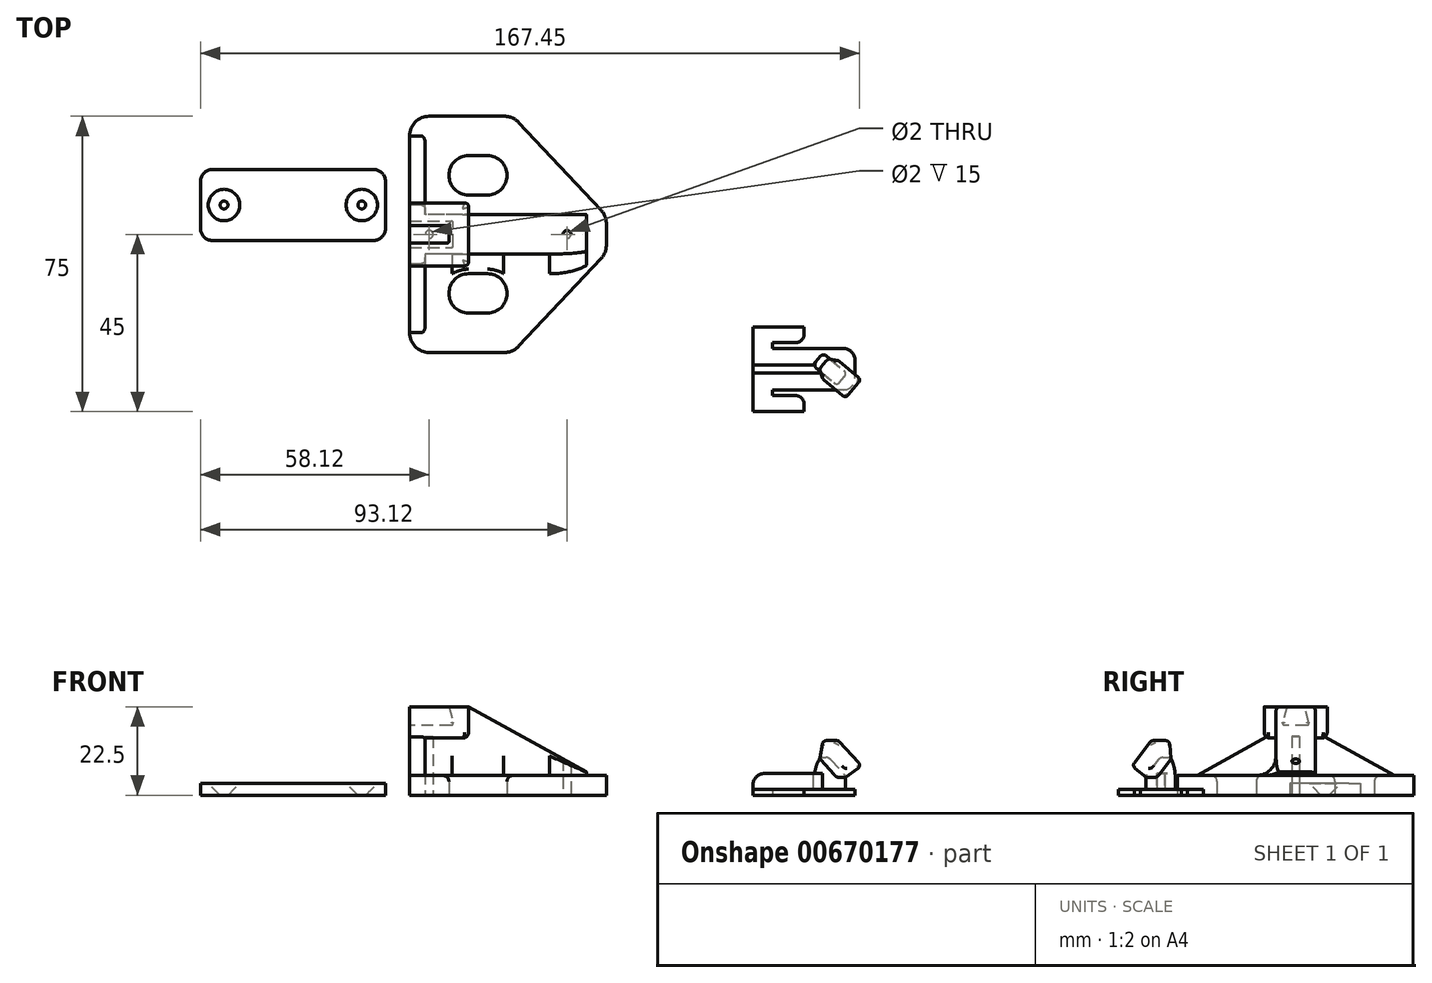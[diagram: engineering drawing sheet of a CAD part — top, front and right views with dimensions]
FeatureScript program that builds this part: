
annotation { "Feature Type Name" : "Feature", "Feature Type Description" : "" }
export const myFeature = defineFeature(function(context is Context, id is Id, definition is map)
    precondition{}
    {
        {
            var Q0;
            Q0=qCreatedBy(makeId("Front.planeOp"),FACE);
            var sketch = newSketch(context, id + "F0", { "sketchPlane" : qUnion([Q0])});
            skLineSegment(sketch, "E0.bottom", {"start": v(-57, 22.5) * mm, "end": v(-42, 22.5) * mm});
            skLineSegment(sketch, "E0.left", {"start": v(-57, 22.5) * mm, "end": v(-57, 0) * mm});
            skLineSegment(sketch, "E1", {"start": v(-42, 22.5) * mm, "end": v(-12, 5.88) * mm});
            skLineSegment(sketch, "E2", {"start": v(-12, 5.88) * mm, "end": v(-12, 0) * mm});
            skLineSegment(sketch, "E3", {"start": v(-12, 0) * mm, "end": v(-57, 0) * mm});
            skSolve(sketch);
        }
        {
            var Q0;
            Q0=makeQuery(id+"F0.imprint","IMPRINT",FACE,{"disambiguationData":[TD([[makeQuery(id+"F0.imprint","IMPRINT",EDGE,{"derivedFrom":sQuery(id+"F0.wireOp",EDGE,"E0.bottom")}),-1.0]])]});
            extrude(context, id + "F1", {"entities" : qUnion([Q0]), "depth" : 10 * mm, "offsetDistance" : 25 * mm, "symmetric" : true});
        }
        {
            var Q0;
            Q0=qCreatedBy(makeId("Top.planeOp"),FACE);
            var sketch = newSketch(context, id + "F2", { "sketchPlane" : qUnion([Q0])});
            skLineSegment(sketch, "E4", {"start": v(-57, 0) * mm, "end": v(-57, -25) * mm});
            skLineSegment(sketch, "E5", {"start": v(-52, -30) * mm, "end": v(-32.9, -30) * mm});
            skLineSegment(sketch, "E6", {"start": v(-29.25, -28.42) * mm, "end": v(-8.35, -6.16) * mm});
            skLineSegment(sketch, "E7", {"start": v(-7, -2.74) * mm, "end": v(-7, 0) * mm});
            skLineSegment(sketch, "E8", {"start": v(-7, 0) * mm, "end": v(-57, 0) * mm});
            skPoint(sketch, "E9.visualSharp", {"position": v(-57, -30) * mm});
            skArc(sketch, "E9.filletArc", {"start": v(-57, -25) * mm, "mid": v(-55.54, -28.54) * mm, "end": v(-52, -30) * mm});
            skPoint(sketch, "E10.visualSharp", {"position": v(-30.73, -30) * mm});
            skArc(sketch, "E10.filletArc", {"start": v(-32.9, -30) * mm, "mid": v(-30.9, -29.59) * mm, "end": v(-29.25, -28.42) * mm});
            skPoint(sketch, "E11.visualSharp", {"position": v(-7, -4.72) * mm});
            skArc(sketch, "E11.filletArc", {"start": v(-8.35, -6.16) * mm, "mid": v(-7.35, -4.58) * mm, "end": v(-7, -2.74) * mm});
            skLineSegment(sketch, "E12.0", {"start": v(-47, -15) * mm, "end": v(-47, -15) * mm});
            skLineSegment(sketch, "E12.1", {"start": v(-37.22, -10) * mm, "end": v(-42, -10) * mm});
            skLineSegment(sketch, "E12.2", {"start": v(-33.58, -18.42) * mm, "end": v(-33.58, -18.42) * mm});
            skLineSegment(sketch, "E12.3", {"start": v(-42, -20) * mm, "end": v(-37.22, -20) * mm});
            skPoint(sketch, "E13.visualSharp", {"position": v(-25.67, -10) * mm});
            skArc(sketch, "E13.filletArc", {"start": v(-33.58, -18.42) * mm, "mid": v(-32.63, -13.01) * mm, "end": v(-37.22, -10) * mm});
            skPoint(sketch, "E14.visualSharp", {"position": v(-47, -10) * mm});
            skArc(sketch, "E14.filletArc", {"start": v(-42, -10) * mm, "mid": v(-45.54, -11.46) * mm, "end": v(-47, -15) * mm});
            skPoint(sketch, "E15.visualSharp", {"position": v(-47, -20) * mm});
            skArc(sketch, "E15.filletArc", {"start": v(-47, -15) * mm, "mid": v(-45.54, -18.54) * mm, "end": v(-42, -20) * mm});
            skPoint(sketch, "E16.visualSharp", {"position": v(-35.06, -20) * mm});
            skArc(sketch, "E16.filletArc", {"start": v(-37.22, -20) * mm, "mid": v(-35.24, -19.59) * mm, "end": v(-33.58, -18.42) * mm});
            skSolve(sketch);
        }
        {
            var Q0;
            Q0=makeQuery(id+"F2.imprint","IMPRINT",FACE,{"disambiguationData":[TD([[makeQuery(id+"F2.imprint","IMPRINT",EDGE,{"derivedFrom":sQuery(id+"F2.wireOp",EDGE,"E4")}),1.0]])]});
            extrude(context, id + "F3", {"entities" : qUnion([Q0]), "operationType" : NewBodyOperationType.ADD, "depth" : 5 * mm, "offsetDistance" : 25 * mm});
        }
        {
            var Q0;
            Q0=makeQuery(id+"F1.opExtrude","SWEPT_BODY",BODY,{"disambiguationData":[OSD([sQuery(id+"F0.wireOp",EDGE,"E0.bottom"),sQuery(id+"F0.wireOp",EDGE,"E0.top"),sQuery(id+"F0.wireOp",EDGE,"E0.left"),sQuery(id+"F0.wireOp",EDGE,"E0.right")])]});
            var Q1;
            Q1=qCreatedBy(makeId("Front.planeOp"),FACE);
            mirror(context, id + "F4", {"operationType" : NewBodyOperationType.ADD, "entities" : qUnion([Q0]), "mirrorPlane" : qUnion([Q1])});
        }
        {
            var Q0;
            Q0=makeQuery(id+"F3.opExtrude","CAP_EDGE",EDGE,{"disambiguationData":[OSD([sQuery(id+"F2.wireOp",EDGE,"E15.filletArc")])],"isStart":false});
            var Q1;
            Q1=makeQuery(id+"F4.opPattern","COPY",EDGE,{"derivedFrom":makeQuery(id+"F3.opExtrude","CAP_EDGE",EDGE,{"disambiguationData":[OSD([sQuery(id+"F2.wireOp",EDGE,"E14.filletArc")])],"isStart":false}),"instanceName":"1"});
            fillet(context, id + "F5", {"entities" : qUnion([Q0, Q1]), "radius" : 1.5 * mm, "tangentPropagation" : true, "allowEdgeOverflow" : false});
        }
        {
            var Q0;
            {var subQ0=makeQuery(id+"F3.boolean.opBoolean","MERGE",FACE,{"derivedFrom":[makeQuery(id+"F1.opExtrude","SWEPT_FACE",FACE,{"disambiguationData":[OSD([sQuery(id+"F0.wireOp",EDGE,"E3")])]}),makeQuery(id+"F3.opExtrude","CAP_FACE",FACE,{"disambiguationData":[OSD([sQuery(id+"F2.wireOp",EDGE,"E4"),sQuery(id+"F2.wireOp",EDGE,"E5"),sQuery(id+"F2.wireOp",EDGE,"E6"),sQuery(id+"F2.wireOp",EDGE,"E7"),sQuery(id+"F2.wireOp",EDGE,"E8"),sQuery(id+"F2.wireOp",EDGE,"E9.filletArc"),sQuery(id+"F2.wireOp",EDGE,"E10.filletArc"),sQuery(id+"F2.wireOp",EDGE,"E11.filletArc"),sQuery(id+"F2.wireOp",EDGE,"E12.0"),sQuery(id+"F2.wireOp",EDGE,"E12.1"),sQuery(id+"F2.wireOp",EDGE,"E12.2"),sQuery(id+"F2.wireOp",EDGE,"E12.3"),sQuery(id+"F2.wireOp",EDGE,"E13.filletArc"),sQuery(id+"F2.wireOp",EDGE,"E14.filletArc"),sQuery(id+"F2.wireOp",EDGE,"E15.filletArc"),sQuery(id+"F2.wireOp",EDGE,"E16.filletArc")])],"isStart":true})]});Q0=makeQuery(id+"F4.boolean.opBoolean","MERGE",FACE,{"derivedFrom":[subQ0,makeQuery(id+"F4.opPattern","COPY",FACE,{"derivedFrom":subQ0,"instanceName":"1"})]});}
            var sketch = newSketch(context, id + "F6", { "sketchPlane" : qUnion([Q0])});
            skLineSegment(sketch, "E17", {"start": v(-57, 0) * mm, "end": v(-7, 0) * mm, "construction": true});
            skCircle(sketch, "E18", {"center": v(-52, 0) * mm, "radius": 1 * mm});
            skCircle(sketch, "E19", {"center": v(-17, 0) * mm, "radius": 1 * mm});
            skSolve(sketch);
        }
        {
            var Q0;
            Q0=makeQuery(id+"F6.imprint","IMPRINT",FACE,{"disambiguationData":[TD([[makeQuery(id+"F6.imprint","IMPRINT",EDGE,{"derivedFrom":sQuery(id+"F6.wireOp",EDGE,"E18")}),1.0]])]});
            var Q1;
            Q1=makeQuery(id+"F6.imprint","IMPRINT",FACE,{"disambiguationData":[TD([[makeQuery(id+"F6.imprint","IMPRINT",EDGE,{"derivedFrom":sQuery(id+"F6.wireOp",EDGE,"E19")}),1.0]])]});
            extrude(context, id + "F7", {"entities" : qUnion([Q0, Q1]), "operationType" : NewBodyOperationType.REMOVE, "oppositeDirection" : true, "depth" : 15 * mm, "offsetDistance" : 25 * mm});
        }
        {
            var Q0;
            {var subQ0=makeQuery(id+"F3.boolean.opBoolean","MERGE",FACE,{"derivedFrom":[makeQuery(id+"F1.opExtrude","SWEPT_FACE",FACE,{"disambiguationData":[OSD([sQuery(id+"F0.wireOp",EDGE,"E0.left")])]}),makeQuery(id+"F3.opExtrude","SWEPT_FACE",FACE,{"disambiguationData":[OSD([sQuery(id+"F2.wireOp",EDGE,"E4")])]})]});Q0=makeQuery(id+"F4.boolean.opBoolean","MERGE",FACE,{"derivedFrom":[subQ0,makeQuery(id+"F4.opPattern","COPY",FACE,{"derivedFrom":subQ0,"instanceName":"1"})]});}
            var sketch = newSketch(context, id + "F8", { "sketchPlane" : qUnion([Q0])});
            skLineSegment(sketch, "E20.bottom", {"start": v(-8, 22.5) * mm, "end": v(8, 22.5) * mm});
            skLineSegment(sketch, "E20.top", {"start": v(-8, 14.5) * mm, "end": v(8, 14.5) * mm});
            skLineSegment(sketch, "E20.left", {"start": v(-8, 22.5) * mm, "end": v(-8, 14.5) * mm});
            skLineSegment(sketch, "E20.right", {"start": v(8, 22.5) * mm, "end": v(8, 14.5) * mm});
            skLineSegment(sketch, "E21", {"start": v(-25, 5) * mm, "end": v(25, 5) * mm});
            skLineSegment(sketch, "E22", {"start": v(-8, 14.5) * mm, "end": v(-25, 5) * mm});
            skLineSegment(sketch, "E23", {"start": v(25, 5) * mm, "end": v(8, 14.5) * mm});
            skSolve(sketch);
        }
        {
            var Q0;
            {var subQ0=sQuery(id+"F8.wireOp",EDGE,"E22");Q0=makeQuery(id+"F8.imprint","IMPRINT",FACE,{"disambiguationData":[TD([[makeQuery(id+"F8.imprint","IMPRINT",EDGE,{"derivedFrom":subQ0}),1.0]])]});}
            var Q1;
            {var subQ0=sQuery(id+"F8.wireOp",EDGE,"E23");Q1=makeQuery(id+"F8.imprint","IMPRINT",FACE,{"disambiguationData":[TD([[makeQuery(id+"F8.imprint","IMPRINT",EDGE,{"derivedFrom":subQ0}),1.0]])]});}
            extrude(context, id + "F9", {"entities" : qUnion([Q0, Q1]), "operationType" : NewBodyOperationType.ADD, "oppositeDirection" : true, "depth" : 4 * mm, "offsetDistance" : 25 * mm});
        }
        {
            var Q0;
            {var subQ3=sQuery(id+"F8.wireOp",EDGE,"E20.left");Q0=makeQuery(id+"F8.imprint","IMPRINT",FACE,{"disambiguationData":[TD([[makeQuery(id+"F8.imprint","IMPRINT",EDGE,{"derivedFrom":subQ3}),1.0]])]});}
            var Q1;
            {var subQ3=sQuery(id+"F8.wireOp",EDGE,"E20.right");Q1=makeQuery(id+"F8.imprint","IMPRINT",FACE,{"disambiguationData":[TD([[makeQuery(id+"F8.imprint","IMPRINT",EDGE,{"derivedFrom":subQ3}),-1.0]])]});}
            extrude(context, id + "F10", {"entities" : qUnion([Q0, Q1]), "operationType" : NewBodyOperationType.ADD, "oppositeDirection" : true, "depth" : 15 * mm, "offsetDistance" : 25 * mm});
        }
        {
            var Q0;
            Q0=makeQuery(id+"F1.opExtrude","CAP_EDGE",EDGE,{"disambiguationData":[OSD([sQuery(id+"F0.wireOp",EDGE,"E1")])],"isStart":true});
            var Q1;
            Q1=makeQuery(id+"F1.opExtrude","CAP_EDGE",EDGE,{"disambiguationData":[OSD([sQuery(id+"F0.wireOp",EDGE,"E1")])],"isStart":false});
            var Q2;
            Q2=makeQuery(id+"F9.opExtrude","CAP_EDGE",EDGE,{"disambiguationData":[OSD([sQuery(id+"F8.wireOp",EDGE,"E23")])],"isStart":false});
            var Q3;
            Q3=makeQuery(id+"F9.opExtrude","CAP_EDGE",EDGE,{"disambiguationData":[OSD([sQuery(id+"F8.wireOp",EDGE,"E22")])],"isStart":false});
            fillet(context, id + "F11", {"entities" : qUnion([Q0, Q1, Q2, Q3]), "radius" : 1 * mm, "tangentPropagation" : true, "allowEdgeOverflow" : false});
        }
        {
            var Q0;
            {var subQ0=sQuery(id+"F8.wireOp",EDGE,"E20.bottom");var subQ1=sQuery(id+"F0.wireOp",EDGE,"E0.left");Q0=makeQuery(id+"F10.boolean.opBoolean","MERGE",FACE,{"derivedFrom":[makeQuery(id+"F1.opExtrude","SWEPT_FACE",FACE,{"disambiguationData":[OSD([sQuery(id+"F0.wireOp",EDGE,"E0.bottom")])]}),makeQuery(id+"F10.opExtrude","SWEPT_FACE",FACE,{"disambiguationData":[OSD([subQ0]),TDD([makeQuery(id+"F8.imprint","IMPRINT",EDGE,{"disambiguationData":[TD([[makeQuery(id+"F8.imprint","INTERSECT",VERTEX,{"derivedFrom":[makeQuery(id+"F1.opExtrude","CAP_EDGE",EDGE,{"disambiguationData":[OSD([subQ1])],"isStart":true}),subQ0]}),1.0],[makeQuery(id+"F8.imprint","INTERSECT",VERTEX,{"derivedFrom":[subQ0,sQuery(id+"F8.wireOp",EDGE,"E20.left")]}),-1.0]])],"derivedFrom":subQ0})])]}),makeQuery(id+"F10.opExtrude","SWEPT_FACE",FACE,{"disambiguationData":[OSD([subQ0]),TDD([makeQuery(id+"F8.imprint","IMPRINT",EDGE,{"disambiguationData":[TD([[makeQuery(id+"F8.imprint","INTERSECT",VERTEX,{"derivedFrom":[makeQuery(id+"F1.opExtrude","CAP_EDGE",EDGE,{"disambiguationData":[OSD([subQ1])],"isStart":false}),subQ0]}),-1.0],[makeQuery(id+"F8.imprint","INTERSECT",VERTEX,{"derivedFrom":[subQ0,sQuery(id+"F8.wireOp",EDGE,"E20.right")]}),1.0]])],"derivedFrom":subQ0})])]})]});}
            var sketch = newSketch(context, id + "F12", { "sketchPlane" : qUnion([Q0])});
            skLineSegment(sketch, "E24", {"start": v(-57, 2.25) * mm, "end": v(-57, -2.25) * mm});
            skLineSegment(sketch, "E25", {"start": v(-57, -2.25) * mm, "end": v(-47, -2.25) * mm});
            skLineSegment(sketch, "E26", {"start": v(-47, -2.25) * mm, "end": v(-47, 2.25) * mm});
            skLineSegment(sketch, "E27", {"start": v(-57, 2.25) * mm, "end": v(-47, 2.25) * mm});
            skSolve(sketch);
        }
        {
            var Q0;
            Q0=makeQuery(id+"F12.imprint","IMPRINT",FACE,{"disambiguationData":[TD([[makeQuery(id+"F12.imprint","IMPRINT",EDGE,{"derivedFrom":sQuery(id+"F12.wireOp",EDGE,"E24")}),-1.0]])]});
            extrude(context, id + "F13", {"entities" : qUnion([Q0]), "operationType" : NewBodyOperationType.REMOVE, "oppositeDirection" : true, "depth" : 4.7 * mm, "offsetDistance" : 25 * mm, "hasDraft" : true, "draftAngle" : 15 * degree});
        }
        {
            var Q0;
            {var subQ0=sQuery(id+"F8.wireOp",EDGE,"E20.top");var subQ1=sQuery(id+"F0.wireOp",EDGE,"E0.left");Q0=makeQuery(id+"F10.opExtrude","SWEPT_EDGE",EDGE,{"disambiguationData":[OSD([subQ1,subQ0]),TDD([makeQuery(id+"F8.imprint","INTERSECT",VERTEX,{"derivedFrom":[makeQuery(id+"F1.opExtrude","CAP_EDGE",EDGE,{"disambiguationData":[OSD([subQ1])],"isStart":false}),subQ0]})])]});}
            var Q1;
            Q1=makeQuery(id+"F10.boolean.opBoolean","SPLIT",EDGE,{"derivedFrom":makeQuery(id+"F10.opExtrude","SWEPT_EDGE",EDGE,{"disambiguationData":[OSD([sQuery(id+"F8.wireOp",EDGE,"E20.top"),sQuery(id+"F8.wireOp",EDGE,"E20.right"),sQuery(id+"F8.wireOp",EDGE,"E23")])]})});
            var Q2;
            {var subQ0=sQuery(id+"F8.wireOp",EDGE,"E20.top");var subQ1=sQuery(id+"F0.wireOp",EDGE,"E0.left");Q2=makeQuery(id+"F10.opExtrude","SWEPT_EDGE",EDGE,{"disambiguationData":[OSD([subQ1,subQ0]),TDD([makeQuery(id+"F8.imprint","INTERSECT",VERTEX,{"derivedFrom":[makeQuery(id+"F1.opExtrude","CAP_EDGE",EDGE,{"disambiguationData":[OSD([subQ1])],"isStart":true}),subQ0]})])]});}
            var Q3;
            Q3=makeQuery(id+"F10.boolean.opBoolean","SPLIT",EDGE,{"derivedFrom":makeQuery(id+"F10.opExtrude","SWEPT_EDGE",EDGE,{"disambiguationData":[OSD([sQuery(id+"F8.wireOp",EDGE,"E20.top"),sQuery(id+"F8.wireOp",EDGE,"E20.left"),sQuery(id+"F8.wireOp",EDGE,"E22")])]})});
            var Q4;
            {var subQ0=sQuery(id+"F8.wireOp",EDGE,"E20.top");Q4=makeQuery(id+"F10.opExtrude","CAP_EDGE",EDGE,{"disambiguationData":[OSD([subQ0]),TDD([makeQuery(id+"F8.imprint","IMPRINT",EDGE,{"disambiguationData":[TD([[makeQuery(id+"F8.imprint","INTERSECT",VERTEX,{"derivedFrom":[makeQuery(id+"F1.opExtrude","CAP_EDGE",EDGE,{"disambiguationData":[OSD([sQuery(id+"F0.wireOp",EDGE,"E0.left")])],"isStart":true}),subQ0]}),1.0]])],"derivedFrom":subQ0})])],"isStart":false});}
            var Q5;
            {var subQ0=sQuery(id+"F8.wireOp",EDGE,"E20.top");Q5=makeQuery(id+"F10.opExtrude","CAP_EDGE",EDGE,{"disambiguationData":[OSD([subQ0]),TDD([makeQuery(id+"F8.imprint","IMPRINT",EDGE,{"disambiguationData":[TD([[makeQuery(id+"F8.imprint","INTERSECT",VERTEX,{"derivedFrom":[makeQuery(id+"F1.opExtrude","CAP_EDGE",EDGE,{"disambiguationData":[OSD([sQuery(id+"F0.wireOp",EDGE,"E0.left")])],"isStart":false}),subQ0]}),-1.0]])],"derivedFrom":subQ0})])],"isStart":false});}
            fillet(context, id + "F14", {"entities" : qUnion([Q0, Q1, Q2, Q3, Q4, Q5]), "radius" : 1.5 * mm, "tangentPropagation" : true, "allowEdgeOverflow" : false});
        }
        {
            var Q0;
            Q0=makeQuery(id+"F1.opExtrude","SWEPT_BODY",BODY,{"disambiguationData":[OSD([sQuery(id+"F0.wireOp",EDGE,"E0.bottom"),sQuery(id+"F0.wireOp",EDGE,"E0.left"),sQuery(id+"F0.wireOp",EDGE,"E1"),sQuery(id+"F0.wireOp",EDGE,"E2"),sQuery(id+"F0.wireOp",EDGE,"E3")])]});
            transform(context, id + "F15", {"entities" : qUnion([Q0]), "transformType" : TransformType.TRANSLATION_3D, "dx" : -10 * mm, "dy" : 0 * mm, "dz" : 0 * mm, "makeCopy" : false});
        }
        {
            var Q0;
            Q0=qCreatedBy(makeId("Top.planeOp"),FACE);
            var sketch = newSketch(context, id + "F16", { "sketchPlane" : qUnion([Q0])});
            skLineSegment(sketch, "E28", {"start": v(-119.13, 7.46) * mm, "end": v(-76.79, 7.46) * mm, "construction": true});
            skCircle(sketch, "E29", {"center": v(-114.13, 7.46) * mm, "radius": 1 * mm});
            skCircle(sketch, "E30", {"center": v(-79.13, 7.46) * mm, "radius": 1 * mm});
            skLineSegment(sketch, "E31.bottom", {"start": v(-117.12, 16.46) * mm, "end": v(-76.12, 16.46) * mm});
            skLineSegment(sketch, "E31.top", {"start": v(-117.12, -1.54) * mm, "end": v(-76.12, -1.54) * mm});
            skLineSegment(sketch, "E31.left", {"start": v(-120.12, 13.46) * mm, "end": v(-120.12, 1.46) * mm});
            skLineSegment(sketch, "E31.right", {"start": v(-73.12, 13.46) * mm, "end": v(-73.12, 1.46) * mm});
            skPoint(sketch, "E32.visualSharp", {"position": v(-120.12, 16.46) * mm});
            skArc(sketch, "E32.filletArc", {"start": v(-117.12, 16.46) * mm, "mid": v(-119.24, 15.58) * mm, "end": v(-120.12, 13.46) * mm});
            skPoint(sketch, "E33.visualSharp", {"position": v(-120.12, -1.54) * mm});
            skArc(sketch, "E33.filletArc", {"start": v(-120.12, 1.46) * mm, "mid": v(-119.24, -0.67) * mm, "end": v(-117.12, -1.54) * mm});
            skPoint(sketch, "E34.visualSharp", {"position": v(-73.12, -1.54) * mm});
            skArc(sketch, "E34.filletArc", {"start": v(-76.12, -1.54) * mm, "mid": v(-74, -0.67) * mm, "end": v(-73.12, 1.46) * mm});
            skPoint(sketch, "E35.visualSharp", {"position": v(-73.12, 16.46) * mm});
            skArc(sketch, "E35.filletArc", {"start": v(-73.12, 13.46) * mm, "mid": v(-74, 15.58) * mm, "end": v(-76.12, 16.46) * mm});
            skSolve(sketch);
        }
        {
            var Q0;
            Q0=makeQuery(id+"F16.imprint","IMPRINT",FACE,{"disambiguationData":[TD([[makeQuery(id+"F16.imprint","IMPRINT",EDGE,{"derivedFrom":sQuery(id+"F16.wireOp",EDGE,"E29")}),1.0]])]});
            var Q1;
            Q1=makeQuery(id+"F16.imprint","IMPRINT",FACE,{"disambiguationData":[TD([[makeQuery(id+"F16.imprint","IMPRINT",EDGE,{"derivedFrom":sQuery(id+"F16.wireOp",EDGE,"E30")}),1.0]])]});
            var Q2;
            Q2=makeQuery(id+"F16.imprint","IMPRINT",FACE,{"disambiguationData":[TD([[makeQuery(id+"F16.imprint","IMPRINT",EDGE,{"derivedFrom":sQuery(id+"F16.wireOp",EDGE,"E29")}),-1.0]])]});
            extrude(context, id + "F17", {"entities" : qUnion([Q0, Q1, Q2]), "depth" : 3 * mm, "offsetDistance" : 25 * mm});
        }
        {
            var Q0;
            Q0=makeQuery(id+"F16.imprint","IMPRINT",FACE,{"disambiguationData":[TD([[makeQuery(id+"F16.imprint","IMPRINT",EDGE,{"derivedFrom":sQuery(id+"F16.wireOp",EDGE,"E29")}),1.0]])]});
            var Q1;
            Q1=makeQuery(id+"F16.imprint","IMPRINT",FACE,{"disambiguationData":[TD([[makeQuery(id+"F16.imprint","IMPRINT",EDGE,{"derivedFrom":sQuery(id+"F16.wireOp",EDGE,"E30")}),1.0]])]});
            extrude(context, id + "F18", {"entities" : qUnion([Q0, Q1]), "operationType" : NewBodyOperationType.REMOVE, "depth" : 5 * mm, "offsetDistance" : 25 * mm, "hasDraft" : true, "draftAngle" : 45 * degree});
        }
        {
            var Q0;
            Q0=qCreatedBy(makeId("Top.planeOp"),FACE);
            var sketch = newSketch(context, id + "F19", { "sketchPlane" : qUnion([Q0])});
            skLineSegment(sketch, "E36", {"start": v(17.57, -34.25) * mm, "end": v(61.33, -34.25) * mm, "construction": true});
            skLineSegment(sketch, "E37", {"start": v(43.19, -29) * mm, "end": v(25.19, -29) * mm});
            skLineSegment(sketch, "E38", {"start": v(25.19, -27.5) * mm, "end": v(31.19, -27.5) * mm});
            skLineSegment(sketch, "E39", {"start": v(33.19, -23.5) * mm, "end": v(20.19, -23.5) * mm});
            skLineSegment(sketch, "E40", {"start": v(25.19, -29) * mm, "end": v(25.19, -27.5) * mm});
            skLineSegment(sketch, "E41", {"start": v(20.19, -23.5) * mm, "end": v(20.19, -34.25) * mm});
            skLineSegment(sketch, "E42", {"start": v(46.19, -32) * mm, "end": v(46.19, -34.25) * mm});
            skLineSegment(sketch, "E43", {"start": v(33.19, -23.5) * mm, "end": v(33.19, -25.5) * mm});
            skPoint(sketch, "E44.visualSharp", {"position": v(46.19, -29) * mm});
            skArc(sketch, "E44.filletArc", {"start": v(46.19, -32) * mm, "mid": v(45.3, -29.88) * mm, "end": v(43.19, -29) * mm});
            skPoint(sketch, "E45.visualSharp", {"position": v(33.19, -27.5) * mm});
            skArc(sketch, "E45.filletArc", {"start": v(31.19, -27.5) * mm, "mid": v(32.6, -26.91) * mm, "end": v(33.19, -25.5) * mm});
            skLineSegment(sketch, "E46", {"start": v(25.19, -29) * mm, "end": v(20.19, -29) * mm});
            skLineSegment(sketch, "E47.MirrorCS", {"start": v(33.19, -45) * mm, "end": v(33.19, -43) * mm});
            skLineSegment(sketch, "E48.MirrorCS", {"start": v(25.19, -39.5) * mm, "end": v(25.19, -41) * mm});
            skArc(sketch, "E49.MirrorCS", {"start": v(31.19, -41) * mm, "mid": v(32.6, -41.58) * mm, "end": v(33.19, -43) * mm});
            skLineSegment(sketch, "E50.MirrorCS", {"start": v(46.19, -36.5) * mm, "end": v(46.19, -34.25) * mm});
            skPoint(sketch, "E51.MirrorP", {"position": v(46.19, -39.5) * mm});
            skLineSegment(sketch, "E52.MirrorCS", {"start": v(25.19, -41) * mm, "end": v(31.19, -41) * mm});
            skLineSegment(sketch, "E53.MirrorCS", {"start": v(43.19, -39.5) * mm, "end": v(25.19, -39.5) * mm});
            skArc(sketch, "E54.MirrorCS", {"start": v(46.19, -36.5) * mm, "mid": v(45.3, -38.62) * mm, "end": v(43.19, -39.5) * mm});
            skLineSegment(sketch, "E55.MirrorCS", {"start": v(20.19, -45) * mm, "end": v(20.19, -34.25) * mm});
            skPoint(sketch, "E56.MirrorP", {"position": v(33.19, -41) * mm});
            skLineSegment(sketch, "E57.MirrorCS", {"start": v(25.19, -39.5) * mm, "end": v(20.19, -39.5) * mm});
            skLineSegment(sketch, "E58.MirrorCS", {"start": v(33.19, -45) * mm, "end": v(20.19, -45) * mm});
            skSolve(sketch);
        }
        {
            var Q0;
            Q0=makeQuery(id+"F19.imprint","IMPRINT",FACE,{"disambiguationData":[TD([[makeQuery(id+"F19.imprint","IMPRINT",EDGE,{"derivedFrom":sQuery(id+"F19.wireOp",EDGE,"E37")}),1.0]])]});
            extrude(context, id + "F20", {"entities" : qUnion([Q0]), "depth" : 1.5 * mm, "offsetDistance" : 25 * mm});
        }
        {
            var Q0;
            Q0=makeQuery(id+"F19.imprint","IMPRINT",FACE,{"disambiguationData":[TD([[makeQuery(id+"F19.imprint","IMPRINT",EDGE,{"derivedFrom":sQuery(id+"F19.wireOp",EDGE,"E38")}),1.0]])]});
            var Q1;
            Q1=makeQuery(id+"F19.imprint","IMPRINT",FACE,{"disambiguationData":[TD([[makeQuery(id+"F19.imprint","IMPRINT",EDGE,{"derivedFrom":sQuery(id+"F19.wireOp",EDGE,"E47.MirrorCS")}),1.0]])]});
            extrude(context, id + "F21", {"entities" : qUnion([Q0, Q1]), "depth" : 1.5 * mm, "offsetDistance" : 25 * mm});
        }
        {
            var Q0;
            Q0=makeQuery(id+"F21.opExtrude","SWEPT_BODY",BODY,{"disambiguationData":[OSD([sQuery(id+"F19.wireOp",EDGE,"E38"),sQuery(id+"F19.wireOp",EDGE,"E39"),sQuery(id+"F19.wireOp",EDGE,"E40"),sQuery(id+"F19.wireOp",EDGE,"E41"),sQuery(id+"F19.wireOp",EDGE,"E43"),sQuery(id+"F19.wireOp",EDGE,"E45.filletArc"),sQuery(id+"F19.wireOp",EDGE,"E46")])]});
            var Q1;
            Q1=makeQuery(id+"F21.opExtrude","SWEPT_BODY",BODY,{"disambiguationData":[OSD([sQuery(id+"F19.wireOp",EDGE,"E47.MirrorCS"),sQuery(id+"F19.wireOp",EDGE,"E48.MirrorCS"),sQuery(id+"F19.wireOp",EDGE,"E49.MirrorCS"),sQuery(id+"F19.wireOp",EDGE,"E52.MirrorCS"),sQuery(id+"F19.wireOp",EDGE,"E55.MirrorCS"),sQuery(id+"F19.wireOp",EDGE,"E57.MirrorCS"),sQuery(id+"F19.wireOp",EDGE,"E58.MirrorCS")])]});
            var Q2;
            Q2=makeQuery(id+"F20.opExtrude","SWEPT_BODY",BODY,{"disambiguationData":[OSD([sQuery(id+"F19.wireOp",EDGE,"E37"),sQuery(id+"F19.wireOp",EDGE,"E41"),sQuery(id+"F19.wireOp",EDGE,"E42"),sQuery(id+"F19.wireOp",EDGE,"E44.filletArc"),sQuery(id+"F19.wireOp",EDGE,"E46"),sQuery(id+"F19.wireOp",EDGE,"E50.MirrorCS"),sQuery(id+"F19.wireOp",EDGE,"E53.MirrorCS"),sQuery(id+"F19.wireOp",EDGE,"E54.MirrorCS"),sQuery(id+"F19.wireOp",EDGE,"E55.MirrorCS"),sQuery(id+"F19.wireOp",EDGE,"E57.MirrorCS")])]});
            booleanBodies(context, id + "F22", {"operationType" : BooleanOperationType.UNION, "tools" : qUnion([Q0, Q1, Q2])});
        }
        {
            var Q0;
            {var subQ0=sQuery(id+"F19.wireOp",EDGE,"E57.MirrorCS");var subQ1=sQuery(id+"F19.wireOp",EDGE,"E55.MirrorCS");var subQ2=sQuery(id+"F19.wireOp",EDGE,"E46");var subQ3=sQuery(id+"F19.wireOp",EDGE,"E41");Q0=makeQuery(id+"F22.opBoolean","MERGE",FACE,{"derivedFrom":[makeQuery(id+"F20.opExtrude","CAP_FACE",FACE,{"disambiguationData":[OSD([sQuery(id+"F19.wireOp",EDGE,"E37"),subQ3,sQuery(id+"F19.wireOp",EDGE,"E42"),sQuery(id+"F19.wireOp",EDGE,"E44.filletArc"),subQ2,sQuery(id+"F19.wireOp",EDGE,"E50.MirrorCS"),sQuery(id+"F19.wireOp",EDGE,"E53.MirrorCS"),sQuery(id+"F19.wireOp",EDGE,"E54.MirrorCS"),subQ1,subQ0])],"isStart":false}),makeQuery(id+"F21.opExtrude","CAP_FACE",FACE,{"disambiguationData":[OSD([sQuery(id+"F19.wireOp",EDGE,"E38"),sQuery(id+"F19.wireOp",EDGE,"E39"),sQuery(id+"F19.wireOp",EDGE,"E40"),subQ3,sQuery(id+"F19.wireOp",EDGE,"E43"),sQuery(id+"F19.wireOp",EDGE,"E45.filletArc"),subQ2])],"isStart":false}),makeQuery(id+"F21.opExtrude","CAP_FACE",FACE,{"disambiguationData":[OSD([sQuery(id+"F19.wireOp",EDGE,"E47.MirrorCS"),sQuery(id+"F19.wireOp",EDGE,"E48.MirrorCS"),sQuery(id+"F19.wireOp",EDGE,"E49.MirrorCS"),sQuery(id+"F19.wireOp",EDGE,"E52.MirrorCS"),subQ1,subQ0,sQuery(id+"F19.wireOp",EDGE,"E58.MirrorCS")])],"isStart":false})]});}
            var sketch = newSketch(context, id + "F23", { "sketchPlane" : qUnion([Q0])});
            skLineSegment(sketch, "E59.bottom", {"start": v(35.49, -33.25) * mm, "end": v(38.06, -30.2) * mm});
            skLineSegment(sketch, "E59.top", {"start": v(41.62, -38.4) * mm, "end": v(44.19, -35.33) * mm});
            skLineSegment(sketch, "E59.left", {"start": v(35.49, -33.25) * mm, "end": v(41.62, -38.4) * mm});
            skLineSegment(sketch, "E59.right", {"start": v(38.06, -30.2) * mm, "end": v(44.19, -35.33) * mm});
            skPoint(sketch, "E60.oppositeSnap0", {"position": v(38.55, -35.83) * mm});
            skLineSegment(sketch, "E60.bottom", {"start": v(20.19, -33.25) * mm, "end": v(35.5, -33.25) * mm});
            skLineSegment(sketch, "E60.top", {"start": v(20.19, -35.25) * mm, "end": v(37.86, -35.25) * mm});
            skLineSegment(sketch, "E60.left", {"start": v(20.19, -33.25) * mm, "end": v(20.19, -35.25) * mm});
            skSolve(sketch);
        }
        {
            var Q0;
            Q0=makeQuery(id+"F23.imprint","IMPRINT",FACE,{"disambiguationData":[TD([[makeQuery(id+"F23.imprint","IMPRINT",EDGE,{"derivedFrom":sQuery(id+"F23.wireOp",EDGE,"E59.bottom")}),-1.0]])]});
            extrude(context, id + "F24", {"entities" : qUnion([Q0]), "operationType" : NewBodyOperationType.ADD, "depth" : 3 * mm, "offsetDistance" : 25 * mm});
        }
        {
            var Q0;
            Q0=makeQuery(id+"F24.opExtrude","CAP_FACE",FACE,{"disambiguationData":[OSD([sQuery(id+"F23.wireOp",EDGE,"E59.bottom"),sQuery(id+"F23.wireOp",EDGE,"E59.top"),sQuery(id+"F23.wireOp",EDGE,"E59.left"),sQuery(id+"F23.wireOp",EDGE,"E59.right")])],"isStart":false});
            var Q1;
            Q1=makeQuery(id+"F24.opExtrude","CAP_EDGE",EDGE,{"disambiguationData":[OSD([sQuery(id+"F23.wireOp",EDGE,"E59.top")])],"isStart":false});
            revolve(context, id + "F25", {"operationType" : NewBodyOperationType.ADD, "surfaceOperationType" : NewSurfaceOperationType.NEW, "entities" : qUnion([Q0]), "axis" : qUnion([Q1]), "revolveType" : RevolveType.ONE_DIRECTION, "angle" : 40 * degree});
        }
        {
            var Q0;
            Q0=makeQuery(id+"F25.opRevolve","CAP_FACE",FACE,{"disambiguationData":[OSD([sQuery(id+"F23.wireOp",EDGE,"E59.bottom"),sQuery(id+"F23.wireOp",EDGE,"E59.top"),sQuery(id+"F23.wireOp",EDGE,"E59.left"),sQuery(id+"F23.wireOp",EDGE,"E59.right")])],"isStart":false});
            extrude(context, id + "F26", {"entities" : qUnion([Q0]), "operationType" : NewBodyOperationType.ADD, "depth" : 5.15 * mm, "offsetDistance" : 25 * mm, "hasDraft" : true, "draftAngle" : 15 * degree});
        }
        {
            var Q0;
            {var subQ1=sQuery(id+"F23.wireOp",EDGE,"E60.bottom");Q0=makeQuery(id+"F23.imprint","IMPRINT",FACE,{"disambiguationData":[TD([[makeQuery(id+"F23.imprint","IMPRINT",EDGE,{"derivedFrom":subQ1}),-1.0]])]});}
            extrude(context, id + "F27", {"entities" : qUnion([Q0]), "operationType" : NewBodyOperationType.ADD, "depth" : 4 * mm, "offsetDistance" : 25 * mm});
        }
        {
            var Q0;
            Q0=makeQuery(id+"F27.opExtrude","CAP_EDGE",EDGE,{"disambiguationData":[OSD([sQuery(id+"F23.wireOp",EDGE,"E60.left")])],"isStart":false});
            fillet(context, id + "F28", {"entities" : qUnion([Q0]), "radius" : 3 * mm, "tangentPropagation" : true, "allowEdgeOverflow" : false});
        }
        {
            var Q0;
            {var subQ0=sQuery(id+"F8.wireOp",EDGE,"E21");Q0=makeQuery(id+"F9.opExtrude","CAP_EDGE",EDGE,{"disambiguationData":[OSD([subQ0]),TDD([makeQuery(id+"F8.imprint","IMPRINT",EDGE,{"disambiguationData":[TD([[makeQuery(id+"F8.imprint","INTERSECT",VERTEX,{"derivedFrom":[makeQuery(id+"F4.opPattern","COPY",EDGE,{"derivedFrom":makeQuery(id+"F3.opExtrude","SWEPT_EDGE",EDGE,{"disambiguationData":[OSD([sQuery(id+"F2.wireOp",EDGE,"E4"),sQuery(id+"F2.wireOp",EDGE,"E9.filletArc")])]}),"instanceName":"1"}),sQuery(id+"F8.wireOp",EDGE,"E22"),subQ0]}),1.0]])],"derivedFrom":subQ0})])],"isStart":false});}
            var Q1;
            Q1=makeQuery(id+"F4.opPattern","COPY",EDGE,{"derivedFrom":makeQuery(id+"F3.boolean.opBoolean","INTERSECT",EDGE,{"derivedFrom":[makeQuery(id+"F1.opExtrude","CAP_FACE",FACE,{"disambiguationData":[OSD([sQuery(id+"F0.wireOp",EDGE,"E0.bottom"),sQuery(id+"F0.wireOp",EDGE,"E0.left"),sQuery(id+"F0.wireOp",EDGE,"E1"),sQuery(id+"F0.wireOp",EDGE,"E2"),sQuery(id+"F0.wireOp",EDGE,"E3")])],"isStart":false}),makeQuery(id+"F3.opExtrude","CAP_FACE",FACE,{"disambiguationData":[OSD([sQuery(id+"F2.wireOp",EDGE,"E4"),sQuery(id+"F2.wireOp",EDGE,"E5"),sQuery(id+"F2.wireOp",EDGE,"E6"),sQuery(id+"F2.wireOp",EDGE,"E7"),sQuery(id+"F2.wireOp",EDGE,"E8"),sQuery(id+"F2.wireOp",EDGE,"E9.filletArc"),sQuery(id+"F2.wireOp",EDGE,"E10.filletArc"),sQuery(id+"F2.wireOp",EDGE,"E11.filletArc"),sQuery(id+"F2.wireOp",EDGE,"E12.1"),sQuery(id+"F2.wireOp",EDGE,"E12.3"),sQuery(id+"F2.wireOp",EDGE,"E13.filletArc"),sQuery(id+"F2.wireOp",EDGE,"E14.filletArc"),sQuery(id+"F2.wireOp",EDGE,"E15.filletArc"),sQuery(id+"F2.wireOp",EDGE,"E16.filletArc")])],"isStart":false})]}),"instanceName":"1"});
            var Q2;
            {var subQ0=sQuery(id+"F8.wireOp",EDGE,"E21");Q2=makeQuery(id+"F9.opExtrude","CAP_EDGE",EDGE,{"disambiguationData":[OSD([subQ0]),TDD([makeQuery(id+"F8.imprint","IMPRINT",EDGE,{"disambiguationData":[TD([[makeQuery(id+"F8.imprint","INTERSECT",VERTEX,{"derivedFrom":[makeQuery(id+"F1.opExtrude","CAP_EDGE",EDGE,{"disambiguationData":[OSD([sQuery(id+"F0.wireOp",EDGE,"E0.left")])],"isStart":false}),subQ0]}),-1.0]])],"derivedFrom":subQ0})])],"isStart":false});}
            var Q3;
            Q3=makeQuery(id+"F3.boolean.opBoolean","INTERSECT",EDGE,{"derivedFrom":[makeQuery(id+"F1.opExtrude","CAP_FACE",FACE,{"disambiguationData":[OSD([sQuery(id+"F0.wireOp",EDGE,"E0.bottom"),sQuery(id+"F0.wireOp",EDGE,"E0.left"),sQuery(id+"F0.wireOp",EDGE,"E1"),sQuery(id+"F0.wireOp",EDGE,"E2"),sQuery(id+"F0.wireOp",EDGE,"E3")])],"isStart":false}),makeQuery(id+"F3.opExtrude","CAP_FACE",FACE,{"disambiguationData":[OSD([sQuery(id+"F2.wireOp",EDGE,"E4"),sQuery(id+"F2.wireOp",EDGE,"E5"),sQuery(id+"F2.wireOp",EDGE,"E6"),sQuery(id+"F2.wireOp",EDGE,"E7"),sQuery(id+"F2.wireOp",EDGE,"E8"),sQuery(id+"F2.wireOp",EDGE,"E9.filletArc"),sQuery(id+"F2.wireOp",EDGE,"E10.filletArc"),sQuery(id+"F2.wireOp",EDGE,"E11.filletArc"),sQuery(id+"F2.wireOp",EDGE,"E12.1"),sQuery(id+"F2.wireOp",EDGE,"E12.3"),sQuery(id+"F2.wireOp",EDGE,"E13.filletArc"),sQuery(id+"F2.wireOp",EDGE,"E14.filletArc"),sQuery(id+"F2.wireOp",EDGE,"E15.filletArc"),sQuery(id+"F2.wireOp",EDGE,"E16.filletArc")])],"isStart":false})]});
            fillet(context, id + "F29", {"entities" : qUnion([Q0, Q1, Q2, Q3]), "tangentPropagation" : true, "radius" : 5 * mm, "defaultsChanged" : false, "vertexSettings" : [], "allowEdgeOverflow" : false});
        }
        {
            var Q0;
            Q0=makeQuery(id+"F13.boolean.opBoolean","COPY",EDGE,{"derivedFrom":makeQuery(id+"F13.opExtrude","SWEPT_EDGE",EDGE,{"disambiguationData":[OSD([sQuery(id+"F12.wireOp",EDGE,"E25"),sQuery(id+"F12.wireOp",EDGE,"E26")])]})});
            var Q1;
            Q1=makeQuery(id+"F13.boolean.opBoolean","COPY",EDGE,{"derivedFrom":makeQuery(id+"F13.opExtrude","SWEPT_EDGE",EDGE,{"disambiguationData":[OSD([sQuery(id+"F12.wireOp",EDGE,"E26"),sQuery(id+"F12.wireOp",EDGE,"E27")])]})});
            var Q2;
            Q2=makeQuery(id+"F13.boolean.opBoolean","COPY",EDGE,{"derivedFrom":makeQuery(id+"F13.opExtrude","CAP_EDGE",EDGE,{"disambiguationData":[OSD([sQuery(id+"F12.wireOp",EDGE,"E25")])],"isStart":false})});
            var Q3;
            Q3=makeQuery(id+"F13.boolean.opBoolean","COPY",EDGE,{"derivedFrom":makeQuery(id+"F13.opExtrude","CAP_EDGE",EDGE,{"disambiguationData":[OSD([sQuery(id+"F12.wireOp",EDGE,"E27")])],"isStart":false})});
            var Q4;
            Q4=makeQuery(id+"F13.boolean.opBoolean","COPY",EDGE,{"derivedFrom":makeQuery(id+"F13.opExtrude","CAP_EDGE",EDGE,{"disambiguationData":[OSD([sQuery(id+"F12.wireOp",EDGE,"E26")])],"isStart":false})});
            fillet(context, id + "F30", {"entities" : qUnion([Q0, Q1, Q2, Q3, Q4]), "tangentPropagation" : true, "radius" : .5 * mm, "defaultsChanged" : false, "vertexSettings" : [], "allowEdgeOverflow" : false});
        }
        {
            var Q0;
            Q0=makeQuery(id+"F26.opExtrude","SWEPT_EDGE",EDGE,{"disambiguationData":[OSD([sQuery(id+"F23.wireOp",EDGE,"E59.bottom"),sQuery(id+"F23.wireOp",EDGE,"E59.right")])]});
            var Q1;
            Q1=makeQuery(id+"F26.opExtrude","SWEPT_EDGE",EDGE,{"disambiguationData":[OSD([sQuery(id+"F23.wireOp",EDGE,"E59.top"),sQuery(id+"F23.wireOp",EDGE,"E59.right")])]});
            var Q2;
            Q2=makeQuery(id+"F26.opExtrude","SWEPT_EDGE",EDGE,{"disambiguationData":[OSD([sQuery(id+"F23.wireOp",EDGE,"E59.top"),sQuery(id+"F23.wireOp",EDGE,"E59.left")])]});
            var Q3;
            Q3=makeQuery(id+"F26.opExtrude","SWEPT_EDGE",EDGE,{"disambiguationData":[OSD([sQuery(id+"F23.wireOp",EDGE,"E59.bottom"),sQuery(id+"F23.wireOp",EDGE,"E59.left")])]});
            var Q4;
            {var subQ0=sQuery(id+"F23.wireOp",EDGE,"E59.left");var subQ1=sQuery(id+"F23.wireOp",EDGE,"E59.bottom");Q4=makeQuery(id+"F27.boolean.opBoolean","SPLIT",EDGE,{"disambiguationData":[topologyDisambiguationEdgeConnected([makeQuery(id+"F24.opExtrude","SWEPT_FACE",FACE,{"disambiguationData":[OSD([subQ0])]})])],"derivedFrom":makeQuery(id+"F25.opRevolve","SWEPT_EDGE",EDGE,{"disambiguationData":[OSD([subQ1,subQ0])]})});}
            var Q5;
            Q5=makeQuery(id+"F25.opRevolve","SWEPT_EDGE",EDGE,{"disambiguationData":[OSD([sQuery(id+"F23.wireOp",EDGE,"E59.bottom"),sQuery(id+"F23.wireOp",EDGE,"E59.right")])]});
            var Q6;
            Q6=makeQuery(id+"F24.opExtrude","SWEPT_EDGE",EDGE,{"disambiguationData":[OSD([sQuery(id+"F23.wireOp",EDGE,"E59.top"),sQuery(id+"F23.wireOp",EDGE,"E59.left")])]});
            var Q7;
            Q7=makeQuery(id+"F24.opExtrude","SWEPT_EDGE",EDGE,{"disambiguationData":[OSD([sQuery(id+"F23.wireOp",EDGE,"E59.top"),sQuery(id+"F23.wireOp",EDGE,"E59.right")])]});
            var Q8;
            Q8=makeQuery(id+"F26.opExtrude","CAP_EDGE",EDGE,{"disambiguationData":[OSD([sQuery(id+"F23.wireOp",EDGE,"E59.left")])],"isStart":false});
            var Q9;
            Q9=makeQuery(id+"F26.opExtrude","CAP_EDGE",EDGE,{"disambiguationData":[OSD([sQuery(id+"F23.wireOp",EDGE,"E59.bottom")])],"isStart":false});
            var Q10;
            Q10=makeQuery(id+"F26.opExtrude","CAP_EDGE",EDGE,{"disambiguationData":[OSD([sQuery(id+"F23.wireOp",EDGE,"E59.top")])],"isStart":false});
            var Q11;
            Q11=makeQuery(id+"F26.opExtrude","CAP_EDGE",EDGE,{"disambiguationData":[OSD([sQuery(id+"F23.wireOp",EDGE,"E59.right")])],"isStart":false});
            fillet(context, id + "F31", {"entities" : qUnion([Q0, Q1, Q2, Q3, Q4, Q5, Q6, Q7, Q8, Q9, Q10, Q11]), "tangentPropagation" : true, "radius" : 1 * mm, "defaultsChanged" : true, "vertexSettings" : [], "allowEdgeOverflow" : false});
        }
        {
            var Q0;
            Q0=makeQuery(id+"F10.opExtrude","CAP_EDGE",EDGE,{"disambiguationData":[OSD([sQuery(id+"F8.wireOp",EDGE,"E20.left")])],"isStart":false});
            var Q1;
            Q1=makeQuery(id+"F10.opExtrude","CAP_EDGE",EDGE,{"disambiguationData":[OSD([sQuery(id+"F8.wireOp",EDGE,"E20.right")])],"isStart":false});
            fillet(context, id + "F32", {"entities" : qUnion([Q0, Q1]), "tangentPropagation" : true, "radius" : 1 * mm, "defaultsChanged" : false, "vertexSettings" : [], "allowEdgeOverflow" : false});
        }
    });
